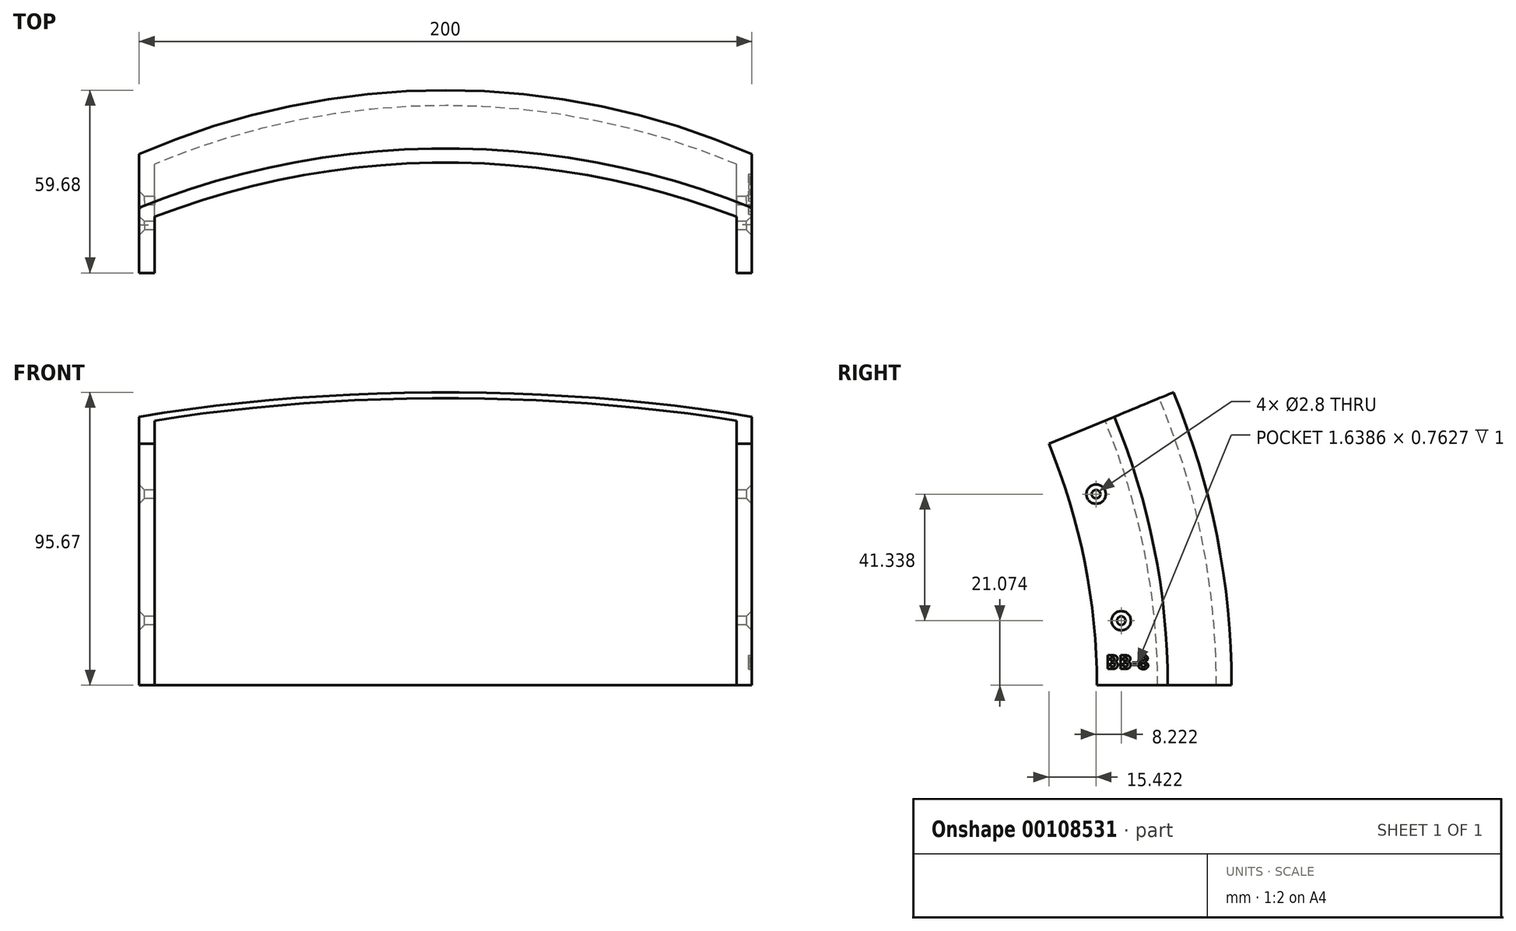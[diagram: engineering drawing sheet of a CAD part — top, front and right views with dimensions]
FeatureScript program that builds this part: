
annotation { "Feature Type Name" : "Feature", "Feature Type Description" : "" }
export const myFeature = defineFeature(function(context is Context, id is Id, definition is map)
    precondition{}
    {
        {
            var Q0;
            Q0=qCreatedBy(makeId("Top.planeOp"),FACE);
            var sketch = newSketch(context, id + "F0", { "sketchPlane" : qUnion([Q0])});
            skArc(sketch, "E0", {"start": v(-95, 225.83) * mm, "mid": v(0, 245) * mm, "end": v(95, 225.83) * mm});
            skArc(sketch, "E1", {"start": v(-100, 229.13) * mm, "mid": v(0, 250) * mm, "end": v(100, 229.13) * mm});
            skLineSegment(sketch, "E2", {"start": v(-100, 229.13) * mm, "end": v(-100, 206) * mm});
            skLineSegment(sketch, "E3", {"start": v(-100, 206) * mm, "end": v(-95, 206) * mm});
            skLineSegment(sketch, "E4", {"start": v(100, 229.13) * mm, "end": v(100, 206) * mm});
            skLineSegment(sketch, "E5", {"start": v(100, 206) * mm, "end": v(95, 206) * mm});
            skLineSegment(sketch, "E6", {"start": v(-95, 0) * mm, "end": v(95, 0) * mm, "construction": true});
            skLineSegment(sketch, "E7", {"start": v(-95, 206) * mm, "end": v(-95, 0) * mm, "construction": true});
            skLineSegment(sketch, "E8", {"start": v(95, 206) * mm, "end": v(95, 225.83) * mm});
            skLineSegment(sketch, "E9", {"start": v(-95, 206) * mm, "end": v(-95, 225.83) * mm});
            skLineSegment(sketch, "E10", {"start": v(95, 0) * mm, "end": v(95, 206) * mm, "construction": true});
            skPoint(sketch, "E11.positionSnap0", {"position": v(0, 225) * mm});
            skLineSegment(sketch, "E12", {"start": v(-95, 225.83) * mm, "end": v(95, 225.83) * mm, "construction": true});
            skPoint(sketch, "E13", {"position": v(0, 225.83) * mm});
            skLineSegment(sketch, "E14", {"start": v(95, 225.83) * mm, "end": v(89.8, 225.83) * mm});
            skLineSegment(sketch, "E15", {"start": v(-95, 225.83) * mm, "end": v(-89.8, 225.83) * mm});
            skLineSegment(sketch, "E16", {"start": v(-89.8, 225.83) * mm, "end": v(-89.8, 220.83) * mm});
            skLineSegment(sketch, "E17", {"start": v(-89.8, 220.83) * mm, "end": v(-85, 220.83) * mm});
            skLineSegment(sketch, "E18", {"start": v(-85, 220.83) * mm, "end": v(-85, 229.78) * mm});
            skLineSegment(sketch, "E19", {"start": v(89.8, 225.83) * mm, "end": v(89.8, 220.83) * mm});
            skLineSegment(sketch, "E20", {"start": v(89.8, 220.83) * mm, "end": v(85, 220.83) * mm});
            skLineSegment(sketch, "E21", {"start": v(85, 220.83) * mm, "end": v(85, 229.78) * mm});
            skSolve(sketch);
        }
        {
            var Q0;
            Q0=makeQuery(id+"F0.imprint","IMPRINT",FACE,{"disambiguationData":[TD([[makeQuery(id+"F0.imprint","IMPRINT",EDGE,{"derivedFrom":sQuery(id+"F0.wireOp",EDGE,"E1")}),-1.0]])]});
            var Q1;
            {var subQ0=sQuery(id+"F0.wireOp",EDGE,"lmNdPizv-3n6S-nKX4-SDGa-ncaC4Ag9tuAc");var subQ1=sQuery(id+"F0.wireOp",EDGE,"E0");var subQ2=makeQuery(id+"F0.imprint","INTERSECT",VERTEX,{"disambiguationData":[OD(0.0)],"derivedFrom":[subQ1,subQ0]});Q1=makeQuery(id+"F0.imprint","IMPRINT",FACE,{"disambiguationData":[TD([[makeQuery(id+"F0.imprint","IMPRINT",EDGE,{"disambiguationData":[TD([[subQ2,-1.0]])],"derivedFrom":subQ1}),-1.0]])]});}
            var Q2;
            {var subQ0=sQuery(id+"F0.wireOp",EDGE,"lmNdPizv-3n6S-nKX4-SDGa-ncaC4Ag9tuAc");var subQ1=sQuery(id+"F0.wireOp",EDGE,"E0");var subQ2=makeQuery(id+"F0.imprint","INTERSECT",VERTEX,{"disambiguationData":[OD(1.0)],"derivedFrom":[subQ1,subQ0]});Q2=makeQuery(id+"F0.imprint","IMPRINT",FACE,{"disambiguationData":[TD([[makeQuery(id+"F0.imprint","IMPRINT",EDGE,{"disambiguationData":[TD([[subQ2,1.0]])],"derivedFrom":subQ1}),-1.0]])]});}
            var Q3;
            {var subQ4=sQuery(id+"F0.wireOp",EDGE,"bwZ3USKc-1TmK-ejq0-4772-UZMCS9pa2qVR");Q3=makeQuery(id+"F0.imprint","IMPRINT",FACE,{"disambiguationData":[TD([[makeQuery(id+"F0.imprint","IMPRINT",EDGE,{"derivedFrom":subQ4}),1.0]])]});}
            var Q4;
            {var subQ4=sQuery(id+"F0.wireOp",EDGE,"LWuvFovu-X8zo-2N0G-cAHU-RIiqH0PJfQXl");Q4=makeQuery(id+"F0.imprint","IMPRINT",FACE,{"disambiguationData":[TD([[makeQuery(id+"F0.imprint","IMPRINT",EDGE,{"derivedFrom":subQ4}),-1.0]])]});}
            var Q5;
            {var subQ0=sQuery(id+"F0.wireOp",EDGE,"pbFOqv5W-1PVb-HM3S-Wum6-j1YJo5w8kIsj");Q5=makeQuery(id+"F0.imprint","IMPRINT",FACE,{"disambiguationData":[TD([[makeQuery(id+"F0.imprint","IMPRINT",EDGE,{"derivedFrom":subQ0}),-1.0]])]});}
            var Q6;
            {var subQ0=sQuery(id+"F0.wireOp",EDGE,"D48Q59Sa-7qnU-lKWU-Bux8-1BkC7HTLLyOH");Q6=makeQuery(id+"F0.imprint","IMPRINT",FACE,{"disambiguationData":[TD([[makeQuery(id+"F0.imprint","IMPRINT",EDGE,{"derivedFrom":subQ0}),1.0]])]});}
            var Q7;
            Q7=sQuery(id+"F0.wireOp",EDGE,"E6");
            revolve(context, id + "F1", {"entities" : qUnion([Q0, Q1, Q2, Q3, Q4, Q5, Q6]), "axis" : qUnion([Q7]), "revolveType" : RevolveType.ONE_DIRECTION, "angle" : 22.5 * degree});
        }
        {
            var Q0;
            Q0=qCreatedBy(makeId("Right.planeOp"),FACE);
            var sketch = newSketch(context, id + "F2", { "sketchPlane" : qUnion([Q0])});
            skLineSegment(sketch, "E22", {"start": v(0, 0) * mm, "end": v(205.74, 62.41) * mm, "construction": true});
            skCircle(sketch, "E23", {"center": v(205.74, 62.41) * mm, "radius": 1.4 * mm});
            skCircle(sketch, "E24.1.0", {"center": v(213.96, 21.07) * mm, "radius": 1.4 * mm});
            skPoint(sketch, "E24.center", {"position": v(0, 0) * mm});
            skLineSegment(sketch, "E24.anchor2", {"start": v(0, 0) * mm, "end": v(213.96, 21.07) * mm, "construction": true});
            skSolve(sketch);
        }
        {
            var Q0;
            Q0=makeQuery(id+"F2.imprint","IMPRINT",FACE,{"disambiguationData":[TD([[makeQuery(id+"F2.imprint","IMPRINT",EDGE,{"derivedFrom":sQuery(id+"F2.wireOp",EDGE,"E23")}),1.0]])]});
            var Q1;
            Q1=makeQuery(id+"F2.imprint","IMPRINT",FACE,{"disambiguationData":[TD([[makeQuery(id+"F2.imprint","IMPRINT",EDGE,{"derivedFrom":sQuery(id+"F2.wireOp",EDGE,"E24.1.0")}),1.0]])]});
            extrude(context, id + "F3", {"entities" : qUnion([Q0, Q1]), "operationType" : NewBodyOperationType.REMOVE, "endBound" : BoundingType.SYMMETRIC, "depth" : 278.72 * mm});
        }
        {
            var Q0;
            Q0=makeQuery(id+"F1.opRevolve","SWEPT_FACE",FACE,{"disambiguationData":[OSD([sQuery(id+"F0.wireOp",EDGE,"E4")])]});
            var sketch = newSketch(context, id + "F4", { "sketchPlane" : qUnion([Q0])});
            skText(sketch, "E25", { "text": "BB-8", "fontName": "OpenSans-Bold.ttf"});
            const initialGuessF4  = {"E25": [0.20896, 0.00532, 1, 0, 0.0045]};
            skSetInitialGuess(sketch, initialGuessF4);
            skSolve(sketch);
        }
        {
            var Q0;
            Q0=qSketchRegion(id+"F4",true);
            extrude(context, id + "F5", {"entities" : qUnion([Q0]), "operationType" : NewBodyOperationType.REMOVE, "oppositeDirection" : true, "depth" : 1 * mm});
        }
        {
            var Q0;
            Q0=makeQuery(id+"F3.boolean.opBoolean","INTERSECT",EDGE,{"derivedFrom":[makeQuery(id+"F1.opRevolve","SWEPT_FACE",FACE,{"disambiguationData":[OSD([sQuery(id+"F0.wireOp",EDGE,"E4")])]}),makeQuery(id+"F3.opExtrude","SWEPT_FACE",FACE,{"disambiguationData":[OSD([sQuery(id+"F2.wireOp",EDGE,"E24.1.0")])]})]});
            var Q1;
            Q1=makeQuery(id+"F3.boolean.opBoolean","INTERSECT",EDGE,{"derivedFrom":[makeQuery(id+"F1.opRevolve","SWEPT_FACE",FACE,{"disambiguationData":[OSD([sQuery(id+"F0.wireOp",EDGE,"E4")])]}),makeQuery(id+"F3.opExtrude","SWEPT_FACE",FACE,{"disambiguationData":[OSD([sQuery(id+"F2.wireOp",EDGE,"E23")])]})]});
            var Q2;
            Q2=makeQuery(id+"F3.boolean.opBoolean","INTERSECT",EDGE,{"derivedFrom":[makeQuery(id+"F1.opRevolve","SWEPT_FACE",FACE,{"disambiguationData":[OSD([sQuery(id+"F0.wireOp",EDGE,"E2")])]}),makeQuery(id+"F3.opExtrude","SWEPT_FACE",FACE,{"disambiguationData":[OSD([sQuery(id+"F2.wireOp",EDGE,"E24.1.0")])]})]});
            var Q3;
            Q3=makeQuery(id+"F3.boolean.opBoolean","INTERSECT",EDGE,{"derivedFrom":[makeQuery(id+"F1.opRevolve","SWEPT_FACE",FACE,{"disambiguationData":[OSD([sQuery(id+"F0.wireOp",EDGE,"E2")])]}),makeQuery(id+"F3.opExtrude","SWEPT_FACE",FACE,{"disambiguationData":[OSD([sQuery(id+"F2.wireOp",EDGE,"E23")])]})]});
            chamfer(context, id + "F6", {"entities" : qUnion([Q0, Q1, Q2, Q3]), "width" : 1.75 * mm, "tangentPropagation" : true});
        }
    });
